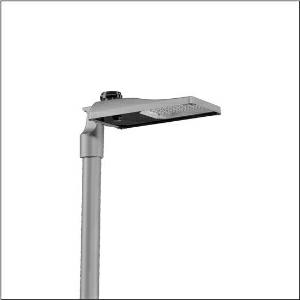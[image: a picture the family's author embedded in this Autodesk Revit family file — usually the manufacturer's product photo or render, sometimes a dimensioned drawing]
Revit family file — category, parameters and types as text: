
# Revit family: streetlight_sl_31_mini___p1_0a_5xh2a35m08ha_3b1d
name_source: partatom
category: Lighting Fixtures
units: mm (PartAtom-declared; Revit-internal decimal feet)

## family parameters
Cut with Voids When Loaded = No
Host = Face
Light Source = No
Part Type = Normal
Room Calculation Point = No
Round Connector Dimension = Use Diameter
Shared = No

## types (1)
- --- (1 x LED, 8970 lm, 68.3 W, 3000K)
    Apparent Load = 68 VA
    CIE Flux Codes = 23 55 94 100 100
    Color Rendering = 70
    Color Temperature = 3000K
    Default Elevation = 1800 mm
    Description = Streetlight SL 31 mini NEMA (7pin), Desk-Remote mast luminaire for post-top, side-entry; light control with lens of PMMA; light distribution: P1.0a, direct asymmetric distribution, for standard-compliant lighting for roads and squares; LED: luminous flux: 8.970lm, light colour: 730, colour temperature: 3000K; luminous efficacy: 131,3lm/W; control: pre-setting: linear dimming characteristic, flexible luminous flux parameterisation, time-dependent luminous flux control, constant luminous flux control, intelligent temperature release in ECG and LED module, overheat protection; luminaire housing, of diecast aluminium, Siteco® metallic grey (DB 702S), corrosivity category C5 high according to DIN EN ISO 12944; cover of toughened safety glass, transparent, mast flange of diecast aluminium, Siteco® metallic grey (DB 702S), spigot size: 76/60mm, mast flange included unmounted; with cable H07RN-F 3x 1.5mm², cable length: 8,5m, connection cable pre-assembled; mains connection: 220..240V, AC, 50/60Hz; power consumption (at start of service life): 68,3W / (at end of service life): 74,5W / (with reduced operation 50%): 29,5W; protection rating (complete): IP66; insulation class (complete): insulation class I (protective earthing); impact resistance: IK09; certification: CE, ENEC, ENEC+, VDE, UKCA; permissible operating ambient temperature for outdoor applications: -40..+50°C; packaging unit: 1 piece

Light Distribution: P1.0a
    Height = 76 mm
    Lamp = 1 x LED
    Lamp Light Flux = 8970 lm
    Lamp Power = 68.3 W
    Lamp count = 1
    Length = 547 mm
    Luminous efficacy = 131 lm/W
    Manufacturer = Siteco
    ModVariant = No
    Model = 5XH2A35M08HA
    Number of Poles = 1
    OnlyDefault = Yes
    Power Factor = 1
    Product Name = Streetlight SL 31 mini | P1.0a
    Product group = mast luminaire | pylon top
    ProductGroupID = 6100
    Protection Class = Protection class I
    Protection Degree = IP 66
    RLX_Detail_Level = 1
    RLX_Emergency_Light_Flux = 0 lm
    RLX_Emergency_Type = 0
    RLX_Emergency_Type_DB = No
    RlxData = <blob elided: 39797 chars, md5=14d2c967>
    Socket = socket
    Standby Power = 0 W
    System Light Flux = 8970 lm
    System Power = 68 W
    Type Comments = factory setting: luminous flux: 100 % | dim-lin: 254 | 692 mA
    Type Image = l_1300324.jpg
    URL = http://relux.com
    VarID = @adj_025653
    Voltage = 0 V
    Weight = 0.00 kg
    Width = 265 mm

## geometry (parser evidence)
native form markers: Blend x4, Sweep x9
no freeform markers — native parametric forms only
